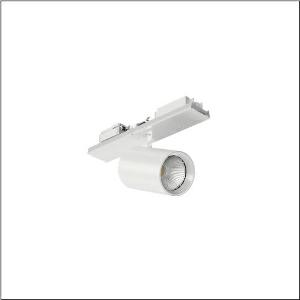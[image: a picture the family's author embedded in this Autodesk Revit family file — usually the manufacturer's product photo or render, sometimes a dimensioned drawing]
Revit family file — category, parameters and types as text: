
# Revit family: licross_r__spot_31_51sl14da45b_0bda
name_source: partatom
category: Lighting Fixtures
units: mm (PartAtom-declared; Revit-internal decimal feet)

## family parameters
Cut with Voids When Loaded = No
Host = Face
Light Source = No
Part Type = Normal
Room Calculation Point = No
Round Connector Dimension = Use Diameter
Shared = No

## types (1)
- --- (1 x LED, 5250 lm, 43.7 W, 4000K)
    Apparent Load = 44 VA
    CIE Flux Codes = 93 97 100 100 100
    Color Rendering = 90
    Color Temperature = 4000K
    Default Elevation = 1800 mm
    Description = Licross® Spot 31, directional spotlight, light control with lens, of plastic, LED rated luminous flux: 5.250lm, light colour: 940, with plug, 5-pole, mains connection: 220..240V, AC, 50/60Hz, of aluminium, traffic white (RAL 9016), length: 140mm, diameter: 90mm, protection rating (complete): IP20, insulation class (complete): insulation class I (protective earthing), certification: CE, packaging unit: 1 piece
    Height = 175 mm
    Lamp = 1 x LED
    Lamp Light Flux = 5250 lm
    Lamp Power = 43.7 W
    Lamp count = 1
    Length = 90 mm
    Luminous efficacy = 120 lm/W
    Manufacturer = Siteco
    ModVariant = No
    Model = 51SL14DA45B
    Mounting Place = Ceiling
    Mounting Type = Pendant
    Number of Poles = 1
    OnlyDefault = Yes
    Power Factor = 1
    Product Name = Licross® Spot 31
    Product group = directional spotlight
    ProductGroupID = 905
    Protection Class = Protection class I
    Protection Degree = IP 20
    RLX_Detail_Level = 1
    RLX_Emergency_Light_Flux = 0 lm
    RLX_Emergency_Type = 0
    RLX_Emergency_Type_DB = No
    RlxData = <blob elided: 14853 chars, md5=b8b0336c>
    Socket = socket
    Standby Power = 0 W
    System Light Flux = 5250 lm
    System Power = 44 W
    Type Comments = factory setting: luminous flux: 100 % | (ON | ON | ON) | 1050 mA
    Type Image = l_1245720.jpg
    URL = http://relux.com
    VarID = @adj_081635
    Voltage = 0 V
    Weight = 0.00 kg
    Width = 0 mm  [stored 0 ft]

note: [stored X ft] marks values corroborated as IEEE doubles in the binary element streams (Revit-internal decimal feet)

## geometry (parser evidence)
native form markers: Sweep x11
no freeform markers — native parametric forms only
